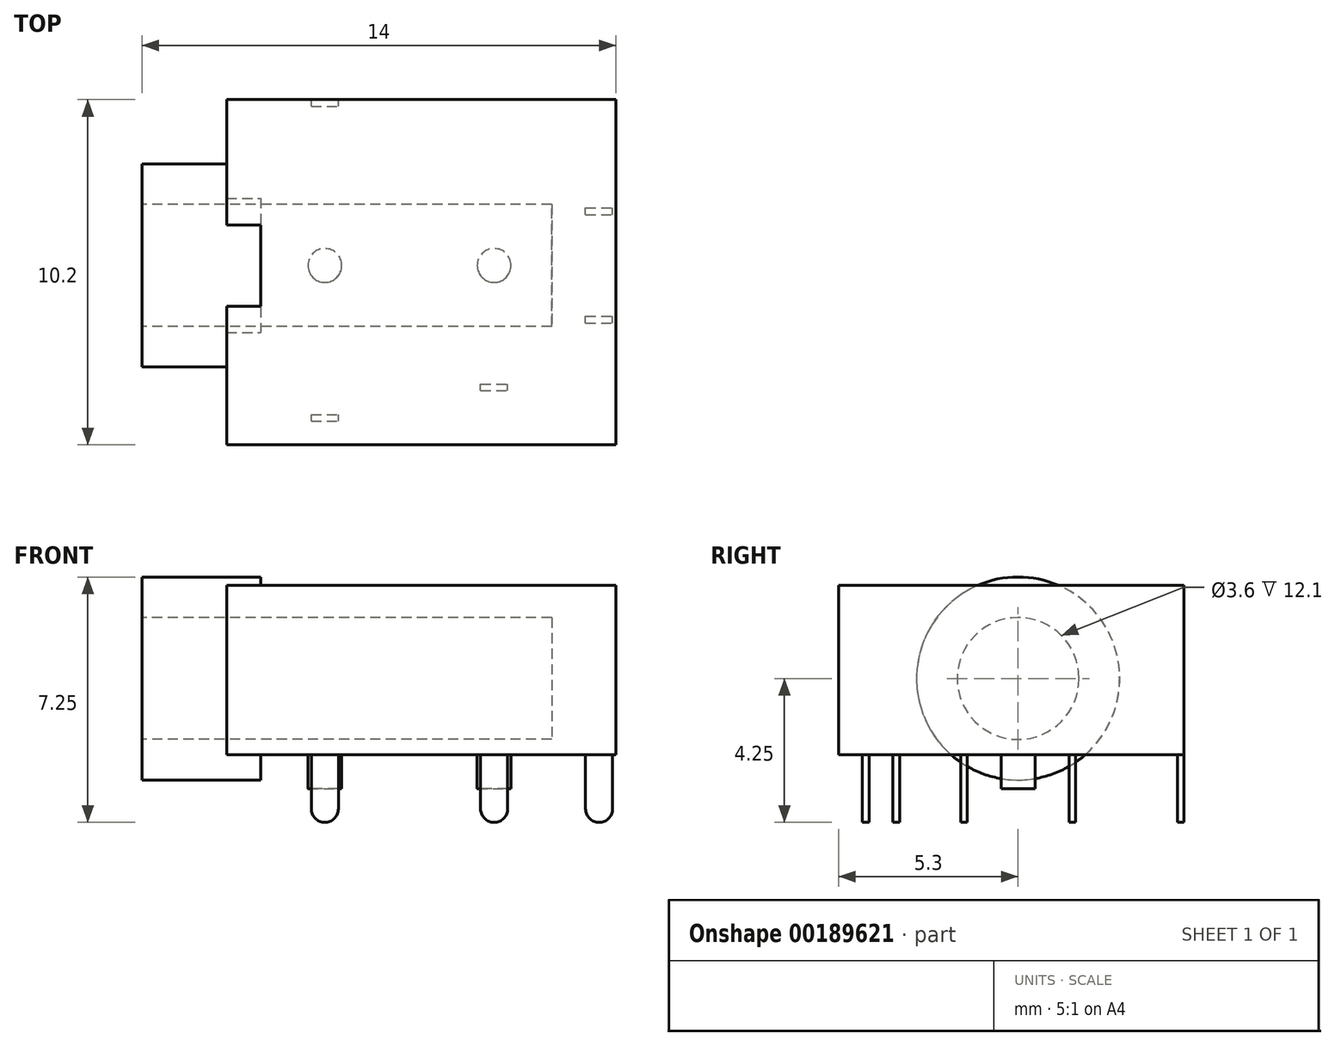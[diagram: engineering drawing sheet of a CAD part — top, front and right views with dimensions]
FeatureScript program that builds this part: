
annotation { "Feature Type Name" : "Feature", "Feature Type Description" : "" }
export const myFeature = defineFeature(function(context is Context, id is Id, definition is map)
    precondition{}
    {
        {
            var Q0;
            Q0=qCreatedBy(makeId("Top.planeOp"),FACE);
            var sketch = newSketch(context, id + "F0", { "sketchPlane" : qUnion([Q0])});
            skLineSegment(sketch, "E0.bottom", {"start": v(0, 4.9) * mm, "end": v(11.5, 4.9) * mm});
            skLineSegment(sketch, "E0.top", {"start": v(0, -5.3) * mm, "end": v(11.5, -5.3) * mm});
            skLineSegment(sketch, "E0.left", {"start": v(0, 4.9) * mm, "end": v(0, -5.3) * mm});
            skLineSegment(sketch, "E0.right", {"start": v(11.5, 4.9) * mm, "end": v(11.5, -5.3) * mm});
            skSolve(sketch);
        }
        {
            var Q0;
            Q0 = qSketchRegion(id + "F0", true);
            extrude(context, id + "F1", {"entities" : qUnion([Q0]), "depth" : 5 * mm});
        }
        {
            var Q0;
            Q0=makeQuery(id+"F1.opExtrude","SWEPT_FACE",FACE,{"disambiguationData":[OSD([sQuery(id+"F0.wireOp",EDGE,"E0.left")])]});
            var sketch = newSketch(context, id + "F2", { "sketchPlane" : qUnion([Q0])});
            skCircle(sketch, "E1", {"center": v(0, 2.25) * mm, "radius": 3 * mm});
            skSolve(sketch);
        }
        {
            var Q0;
            Q0 = qSketchRegion(id + "F2", true);
            extrude(context, id + "F3", {"entities" : qUnion([Q0]), "operationType" : NewBodyOperationType.ADD, "depth" : 2.5 * mm, "hasSecondDirection" : true, "secondDirectionOppositeDirection" : true, "secondDirectionDepth" : 1 * mm});
        }
        {
            var Q0;
            Q0=makeQuery(id+"F3.opExtrude","CAP_FACE",FACE,{"disambiguationData":[OSD([sQuery(id+"F2.wireOp",EDGE,"E1")])],"isStart":false});
            var sketch = newSketch(context, id + "F4", { "sketchPlane" : qUnion([Q0])});
            skCircle(sketch, "E2", {"center": v(0, 2.25) * mm, "radius": 1.8 * mm});
            skSolve(sketch);
        }
        {
            var Q0;
            Q0 = qSketchRegion(id + "F4", true);
            extrude(context, id + "F5", {"entities" : qUnion([Q0]), "operationType" : NewBodyOperationType.REMOVE, "oppositeDirection" : true, "depth" : 12.1 * mm});
        }
        {
            var Q0;
            Q0=makeQuery(id+"F1.opExtrude","CAP_FACE",FACE,{"disambiguationData":[OSD([sQuery(id+"F0.wireOp",EDGE,"E0.bottom"),sQuery(id+"F0.wireOp",EDGE,"E0.top"),sQuery(id+"F0.wireOp",EDGE,"E0.left"),sQuery(id+"F0.wireOp",EDGE,"E0.right")])],"isStart":true});
            var sketch = newSketch(context, id + "F6", { "sketchPlane" : qUnion([Q0])});
            skCircle(sketch, "E3", {"center": v(2.9, 0) * mm, "radius": 0.5 * mm});
            skCircle(sketch, "E4", {"center": v(7.9, 0) * mm, "radius": 0.5 * mm});
            skSolve(sketch);
        }
        {
            var Q0;
            Q0 = qSketchRegion(id + "F6", true);
            extrude(context, id + "F7", {"entities" : qUnion([Q0]), "operationType" : NewBodyOperationType.ADD, "depth" : 1 * mm});
        }
        {
            var Q0;
            Q0=qCreatedBy(makeId("Front.planeOp"),FACE);
            var sketch = newSketch(context, id + "F8", { "sketchPlane" : qUnion([Q0])});
            skLineSegment(sketch, "E5.bottom", {"start": v(-0.4, 0) * mm, "end": v(0.4, 0) * mm});
            skLineSegment(sketch, "E5.top", {"start": v(0, -2) * mm, "end": v(0, -2) * mm});
            skLineSegment(sketch, "E5.left", {"start": v(-0.4, 0) * mm, "end": v(-0.4, -1.6) * mm});
            skLineSegment(sketch, "E5.right", {"start": v(0.4, 0) * mm, "end": v(0.4, -1.6) * mm});
            skPoint(sketch, "E6.visualSharp", {"position": v(-0.4, -2) * mm});
            skArc(sketch, "E6.filletArc", {"start": v(-0.4, -1.6) * mm, "mid": v(-0.28, -1.88) * mm, "end": v(0, -2) * mm});
            skPoint(sketch, "E7.visualSharp", {"position": v(0.4, -2) * mm});
            skArc(sketch, "E7.filletArc", {"start": v(0, -2) * mm, "mid": v(0.28, -1.88) * mm, "end": v(0.4, -1.6) * mm});
            skPoint(sketch, "E8", {"position": v(0, 0) * mm});
            skSolve(sketch);
        }
        {
            var Q0;
            Q0 = qSketchRegion(id + "F8", true);
            extrude(context, id + "F9", {"entities" : qUnion([Q0]), "depth" : 0.2 * mm, "symmetric" : true});
        }
        {
            var Q0;
            Q0=makeQuery(id+"F9.opExtrude","SWEPT_BODY",BODY,{"disambiguationData":[OSD([sQuery(id+"F8.wireOp",EDGE,"E5.bottom"),sQuery(id+"F8.wireOp",EDGE,"E5.left"),sQuery(id+"F8.wireOp",EDGE,"E5.right"),sQuery(id+"F8.wireOp",EDGE,"E6.filletArc"),sQuery(id+"F8.wireOp",EDGE,"E7.filletArc")])]});
            transform(context, id + "F10", {"entities" : qUnion([Q0]), "transformType" : TransformType.TRANSLATION_3D, "dx" : 2.9 * mm, "dy" : 4.8 * mm, "dz" : 0 * mm, "makeCopy" : true});
        }
        {
            var Q0;
            Q0=makeQuery(id+"F9.opExtrude","SWEPT_BODY",BODY,{"disambiguationData":[OSD([sQuery(id+"F8.wireOp",EDGE,"E5.bottom"),sQuery(id+"F8.wireOp",EDGE,"E5.left"),sQuery(id+"F8.wireOp",EDGE,"E5.right"),sQuery(id+"F8.wireOp",EDGE,"E6.filletArc"),sQuery(id+"F8.wireOp",EDGE,"E7.filletArc")])]});
            transform(context, id + "F11", {"entities" : qUnion([Q0]), "transformType" : TransformType.TRANSLATION_3D, "dx" : 2.9 * mm, "dy" : -4.5 * mm, "dz" : 0 * mm, "makeCopy" : true});
        }
        {
            var Q0;
            Q0=makeQuery(id+"F9.opExtrude","SWEPT_BODY",BODY,{"disambiguationData":[OSD([sQuery(id+"F8.wireOp",EDGE,"E5.bottom"),sQuery(id+"F8.wireOp",EDGE,"E5.left"),sQuery(id+"F8.wireOp",EDGE,"E5.right"),sQuery(id+"F8.wireOp",EDGE,"E6.filletArc"),sQuery(id+"F8.wireOp",EDGE,"E7.filletArc")])]});
            transform(context, id + "F12", {"entities" : qUnion([Q0]), "transformType" : TransformType.TRANSLATION_3D, "dx" : 11 * mm, "dy" : 1.6 * mm, "dz" : 0 * mm, "makeCopy" : true});
        }
        {
            var Q0;
            Q0=makeQuery(id+"F9.opExtrude","SWEPT_BODY",BODY,{"disambiguationData":[OSD([sQuery(id+"F8.wireOp",EDGE,"E5.bottom"),sQuery(id+"F8.wireOp",EDGE,"E5.left"),sQuery(id+"F8.wireOp",EDGE,"E5.right"),sQuery(id+"F8.wireOp",EDGE,"E6.filletArc"),sQuery(id+"F8.wireOp",EDGE,"E7.filletArc")])]});
            transform(context, id + "F13", {"entities" : qUnion([Q0]), "transformType" : TransformType.TRANSLATION_3D, "dx" : 11 * mm, "dy" : -1.6 * mm, "dz" : 0 * mm, "makeCopy" : true});
        }
        {
            var Q0;
            Q0=makeQuery(id+"F9.opExtrude","SWEPT_BODY",BODY,{"disambiguationData":[OSD([sQuery(id+"F8.wireOp",EDGE,"E5.bottom"),sQuery(id+"F8.wireOp",EDGE,"E5.left"),sQuery(id+"F8.wireOp",EDGE,"E5.right"),sQuery(id+"F8.wireOp",EDGE,"E6.filletArc"),sQuery(id+"F8.wireOp",EDGE,"E7.filletArc")])]});
            transform(context, id + "F14", {"entities" : qUnion([Q0]), "transformType" : TransformType.TRANSLATION_3D, "dx" : 7.9 * mm, "dy" : -3.6 * mm, "dz" : 0 * mm, "makeCopy" : false});
        }
    });
